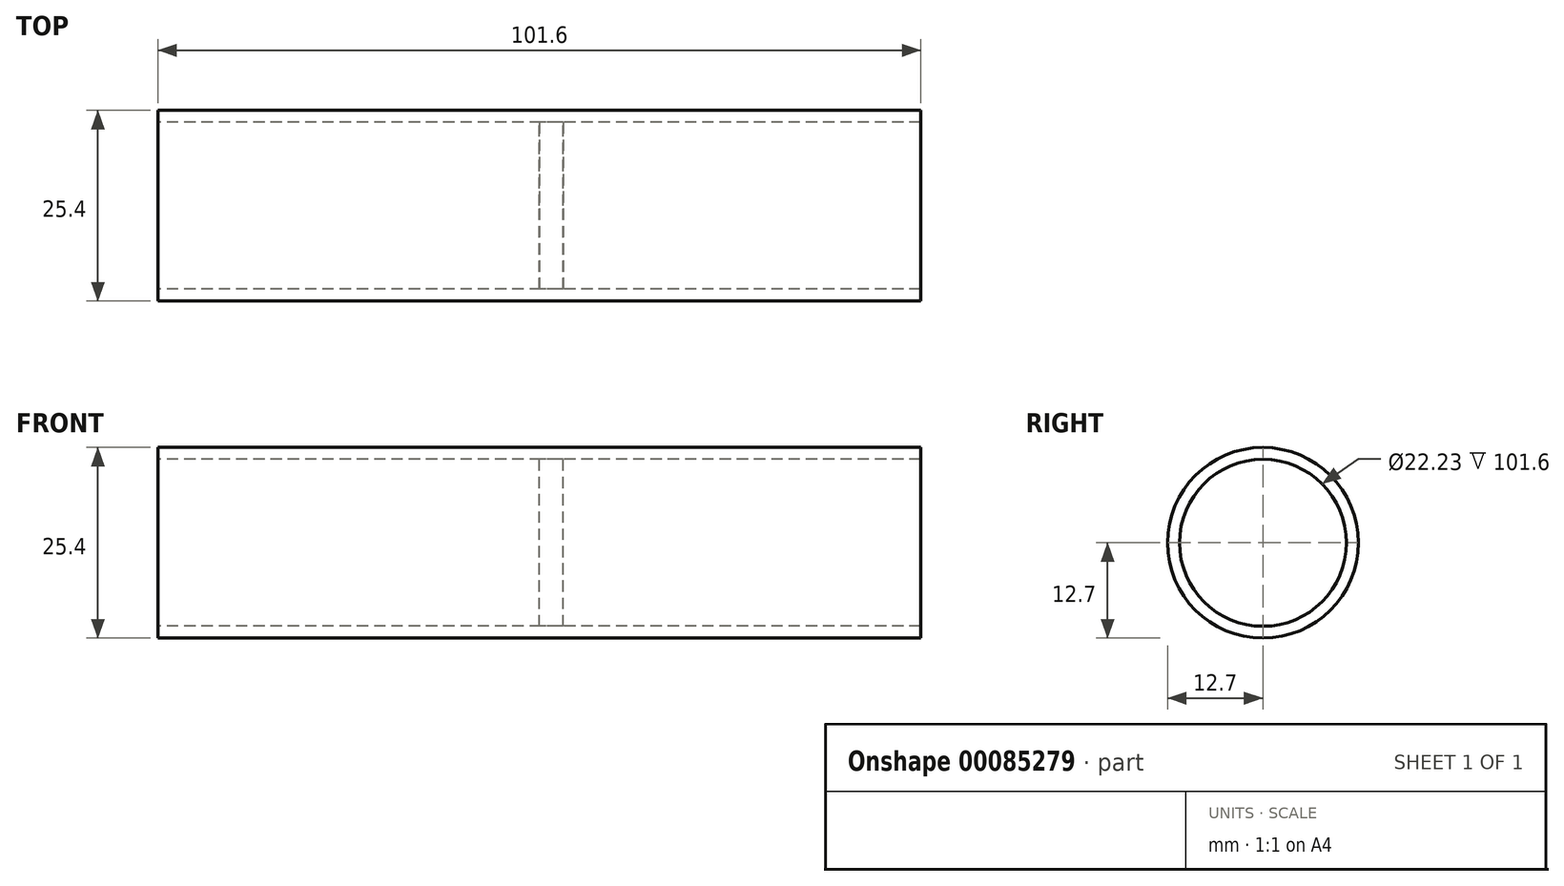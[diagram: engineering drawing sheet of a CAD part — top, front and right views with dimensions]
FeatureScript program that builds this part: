
annotation { "Feature Type Name" : "Feature", "Feature Type Description" : "" }
export const myFeature = defineFeature(function(context is Context, id is Id, definition is map)
    precondition{}
    {
        {
            var Q0;
            Q0=qCreatedBy(makeId("Right.planeOp"),FACE);
            var sketch = newSketch(context, id + "F0", { "sketchPlane" : qUnion([Q0])});
            skCircle(sketch, "E0", {"center": v(0, 0) * mm, "radius": 12.7 * mm});
            skCircle(sketch, "E1", {"center": v(0, 0) * mm, "radius": 11.11 * mm});
            skSolve(sketch);
        }
        {
            var Q0;
            Q0=makeQuery(id+"F0.imprint","IMPRINT",FACE,{"disambiguationData":[TD([[makeQuery(id+"F0.imprint","IMPRINT",EDGE,{"derivedFrom":sQuery(id+"F0.wireOp",EDGE,"E0")}),1.0]])]});
            extrude(context, id + "F1", {"entities" : qUnion([Q0]), "depth" : 101.6 * mm});
        }
        {
            var Q0;
            Q0=qCreatedBy(makeId("Right.planeOp"),FACE);
            cPlane(context, id + "F2", {"entities" : qUnion([Q0]), "cplaneType" : CPlaneType.OFFSET, "offset" : 50.8 * mm, "width" : 152.4 * mm, "height" : 152.4 * mm});
        }
        {
            var Q0;
            Q0=qCreatedBy(id+"F2.planeOp",FACE);
            var sketch = newSketch(context, id + "F3", { "sketchPlane" : qUnion([Q0])});
            skCircle(sketch, "E2", {"center": v(0, 0) * mm, "radius": 11.11 * mm});
            skSolve(sketch);
        }
        {
            var Q0;
            Q0=makeQuery(id+"F3.imprint","IMPRINT",FACE,{"disambiguationData":[TD([[makeQuery(id+"F3.imprint","IMPRINT",EDGE,{"derivedFrom":sQuery(id+"F3.wireOp",EDGE,"E2")}),1.0]])]});
            extrude(context, id + "F4", {"entities" : qUnion([Q0]), "depth" : 3.17 * mm});
        }
    });
